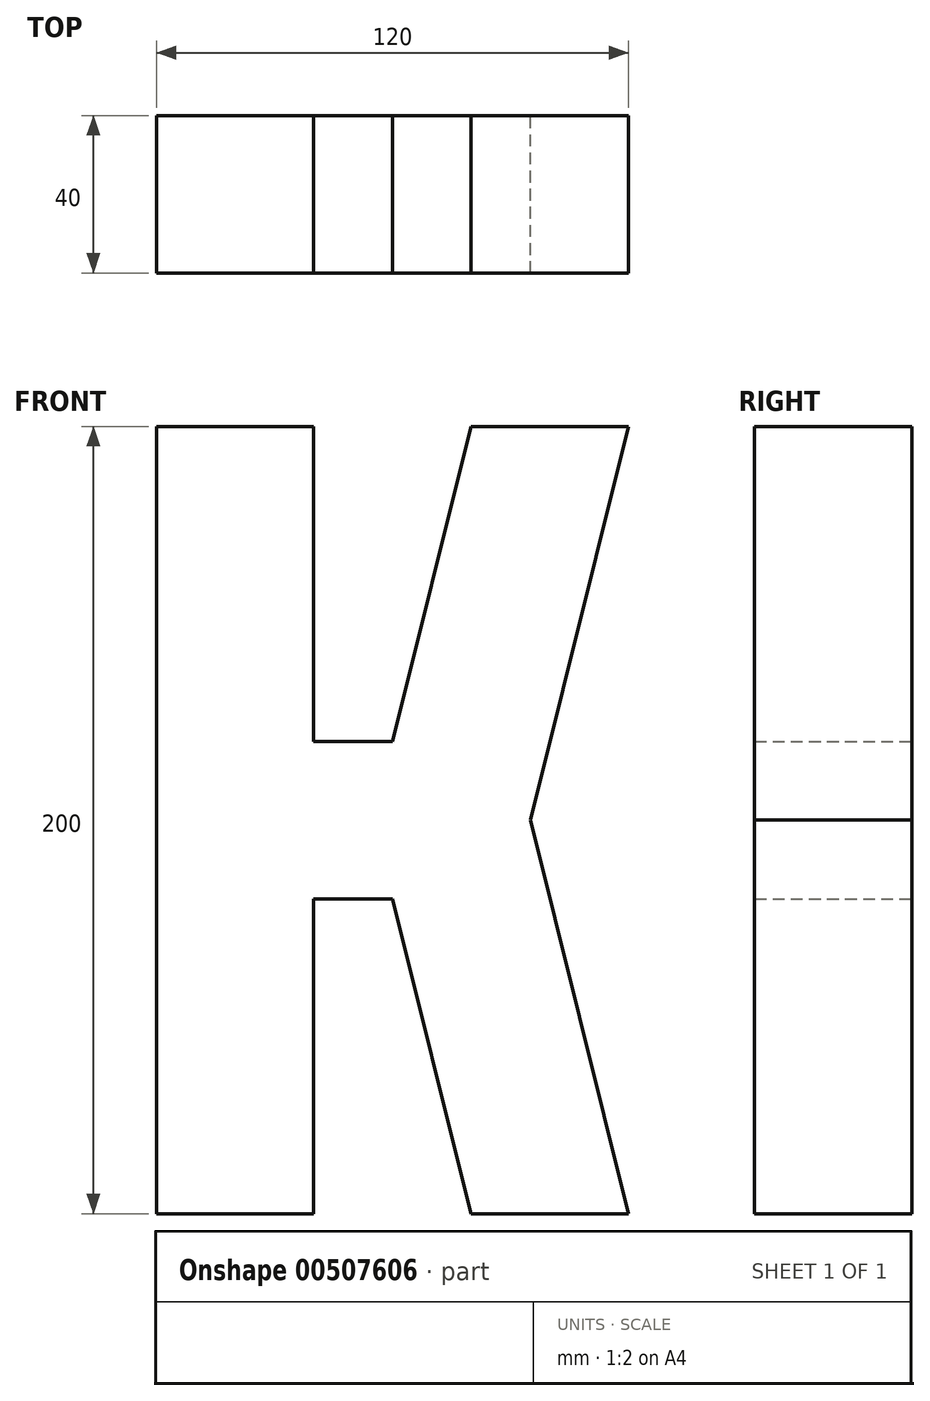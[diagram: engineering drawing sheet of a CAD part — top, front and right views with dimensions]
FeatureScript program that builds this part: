
annotation { "Feature Type Name" : "Feature", "Feature Type Description" : "" }
export const myFeature = defineFeature(function(context is Context, id is Id, definition is map)
    precondition{}
    {
        {
            var Q0;
            Q0=qCreatedBy(makeId("Front.planeOp"),FACE);
            var sketch = newSketch(context, id + "F0", { "sketchPlane" : qUnion([Q0])});
            skLineSegment(sketch, "E0.bottom", {"start": v(60, 100) * mm, "end": v(-60, 100) * mm});
            skLineSegment(sketch, "E0.top", {"start": v(60, -100) * mm, "end": v(-60, -100) * mm});
            skLineSegment(sketch, "E0.left", {"start": v(60, 100) * mm, "end": v(60, -100) * mm});
            skLineSegment(sketch, "E0.right", {"start": v(-60, 100) * mm, "end": v(-60, -100) * mm});
            skPoint(sketch, "E0.middle", {"position": v(0, 0) * mm});
            skLineSegment(sketch, "E1", {"start": v(-20, 100) * mm, "end": v(-20, -100) * mm});
            skLineSegment(sketch, "E2", {"start": v(20, 100) * mm, "end": v(20, -100) * mm});
            skLineSegment(sketch, "E3", {"start": v(60, 60) * mm, "end": v(-60, 60) * mm});
            skLineSegment(sketch, "E4", {"start": v(60, 20) * mm, "end": v(-60, 20) * mm});
            skLineSegment(sketch, "E5", {"start": v(60, -20) * mm, "end": v(-60, -20) * mm});
            skLineSegment(sketch, "E6", {"start": v(60, -60) * mm, "end": v(-60, -60) * mm});
            skPoint(sketch, "E7", {"position": v(0, 100) * mm});
            skLineSegment(sketch, "E8", {"start": v(0, 20) * mm, "end": v(20, 100) * mm});
            skLineSegment(sketch, "E9", {"start": v(60, 100) * mm, "end": v(35, 0) * mm});
            skLineSegment(sketch, "E10.MirrorCS", {"start": v(0, -20) * mm, "end": v(20, -100) * mm});
            skLineSegment(sketch, "E11.MirrorCS", {"start": v(60, -100) * mm, "end": v(35, 0) * mm});
            skSolve(sketch);
        }
        {
            var Q0;
            {var subQ0=sQuery(id+"F0.wireOp",EDGE,"E0.right");var subQ1=sQuery(id+"F0.wireOp",EDGE,"E0.bottom");var subQ2=makeQuery(id+"F0.imprint","INTERSECT",VERTEX,{"derivedFrom":[subQ1,subQ0]});Q0=makeQuery(id+"F0.imprint","IMPRINT",FACE,{"disambiguationData":[TD([[makeQuery(id+"F0.imprint","IMPRINT",EDGE,{"disambiguationData":[TD([[subQ2,1.0]])],"derivedFrom":subQ1}),1.0]])]});}
            var Q1;
            {var subQ0=sQuery(id+"F0.wireOp",EDGE,"E3");var subQ1=sQuery(id+"F0.wireOp",EDGE,"E0.right");var subQ2=makeQuery(id+"F0.imprint","INTERSECT",VERTEX,{"derivedFrom":[subQ1,subQ0]});Q1=makeQuery(id+"F0.imprint","IMPRINT",FACE,{"disambiguationData":[TD([[makeQuery(id+"F0.imprint","IMPRINT",EDGE,{"disambiguationData":[TD([[subQ2,-1.0]])],"derivedFrom":subQ1}),1.0]])]});}
            var Q2;
            {var subQ0=sQuery(id+"F0.wireOp",EDGE,"E4");var subQ1=sQuery(id+"F0.wireOp",EDGE,"E0.right");var subQ2=makeQuery(id+"F0.imprint","INTERSECT",VERTEX,{"derivedFrom":[subQ1,subQ0]});Q2=makeQuery(id+"F0.imprint","IMPRINT",FACE,{"disambiguationData":[TD([[makeQuery(id+"F0.imprint","IMPRINT",EDGE,{"disambiguationData":[TD([[subQ2,-1.0]])],"derivedFrom":subQ1}),1.0]])]});}
            var Q3;
            {var subQ0=sQuery(id+"F0.wireOp",EDGE,"E5");var subQ1=sQuery(id+"F0.wireOp",EDGE,"E0.right");var subQ2=makeQuery(id+"F0.imprint","INTERSECT",VERTEX,{"derivedFrom":[subQ1,subQ0]});Q3=makeQuery(id+"F0.imprint","IMPRINT",FACE,{"disambiguationData":[TD([[makeQuery(id+"F0.imprint","IMPRINT",EDGE,{"disambiguationData":[TD([[subQ2,-1.0]])],"derivedFrom":subQ1}),1.0]])]});}
            var Q4;
            {var subQ0=sQuery(id+"F0.wireOp",EDGE,"E0.right");var subQ1=sQuery(id+"F0.wireOp",EDGE,"E0.top");var subQ2=makeQuery(id+"F0.imprint","INTERSECT",VERTEX,{"derivedFrom":[subQ1,subQ0]});Q4=makeQuery(id+"F0.imprint","IMPRINT",FACE,{"disambiguationData":[TD([[makeQuery(id+"F0.imprint","IMPRINT",EDGE,{"disambiguationData":[TD([[subQ2,1.0]])],"derivedFrom":subQ1}),-1.0]])]});}
            var Q5;
            {var subQ0=sQuery(id+"F0.wireOp",EDGE,"E4");var subQ2=sQuery(id+"F0.wireOp",EDGE,"E1");var subQ3=makeQuery(id+"F0.imprint","INTERSECT",VERTEX,{"derivedFrom":[subQ2,subQ0]});Q5=makeQuery(id+"F0.imprint","IMPRINT",FACE,{"disambiguationData":[TD([[makeQuery(id+"F0.imprint","IMPRINT",EDGE,{"disambiguationData":[TD([[subQ3,-1.0]])],"derivedFrom":subQ2}),1.0]])]});}
            var Q6;
            {var subQ3=sQuery(id+"F0.wireOp",EDGE,"E4");var subQ6=sQuery(id+"F0.wireOp",EDGE,"E2");var subQ9=makeQuery(id+"F0.imprint","INTERSECT",VERTEX,{"derivedFrom":[subQ6,subQ3]});Q6=makeQuery(id+"F0.imprint","IMPRINT",FACE,{"disambiguationData":[TD([[makeQuery(id+"F0.imprint","IMPRINT",EDGE,{"disambiguationData":[TD([[subQ9,-1.0]])],"derivedFrom":subQ6}),1.0]])]});}
            var Q7;
            {var subQ0=sQuery(id+"F0.wireOp",EDGE,"E5");var subQ1=sQuery(id+"F0.wireOp",EDGE,"E2");var subQ2=makeQuery(id+"F0.imprint","INTERSECT",VERTEX,{"derivedFrom":[subQ1,subQ0]});Q7=makeQuery(id+"F0.imprint","IMPRINT",FACE,{"disambiguationData":[TD([[makeQuery(id+"F0.imprint","IMPRINT",EDGE,{"disambiguationData":[TD([[subQ2,-1.0]])],"derivedFrom":subQ1}),1.0]])]});}
            var Q8;
            {var subQ3=sQuery(id+"F0.wireOp",EDGE,"E2");var subQ5=sQuery(id+"F0.wireOp",EDGE,"E6");var subQ7=makeQuery(id+"F0.imprint","INTERSECT",VERTEX,{"derivedFrom":[subQ3,subQ5]});Q8=makeQuery(id+"F0.imprint","IMPRINT",FACE,{"disambiguationData":[TD([[makeQuery(id+"F0.imprint","IMPRINT",EDGE,{"disambiguationData":[TD([[subQ7,1.0]])],"derivedFrom":subQ5}),1.0]])]});}
            var Q9;
            {var subQ0=sQuery(id+"F0.wireOp",EDGE,"E5");var subQ1=sQuery(id+"F0.wireOp",EDGE,"E2");var subQ2=makeQuery(id+"F0.imprint","INTERSECT",VERTEX,{"derivedFrom":[subQ1,subQ0]});Q9=makeQuery(id+"F0.imprint","IMPRINT",FACE,{"disambiguationData":[TD([[makeQuery(id+"F0.imprint","IMPRINT",EDGE,{"disambiguationData":[TD([[subQ2,-1.0]])],"derivedFrom":subQ1}),-1.0]])]});}
            var Q10;
            {var subQ1=sQuery(id+"F0.wireOp",EDGE,"E2");var subQ3=sQuery(id+"F0.wireOp",EDGE,"E6");var subQ4=makeQuery(id+"F0.imprint","INTERSECT",VERTEX,{"derivedFrom":[subQ1,subQ3]});Q10=makeQuery(id+"F0.imprint","IMPRINT",FACE,{"disambiguationData":[TD([[makeQuery(id+"F0.imprint","IMPRINT",EDGE,{"disambiguationData":[TD([[subQ4,-1.0]])],"derivedFrom":subQ3}),1.0]])]});}
            var Q11;
            {var subQ0=sQuery(id+"F0.wireOp",EDGE,"E3");var subQ1=sQuery(id+"F0.wireOp",EDGE,"E2");var subQ2=makeQuery(id+"F0.imprint","INTERSECT",VERTEX,{"derivedFrom":[subQ1,subQ0]});Q11=makeQuery(id+"F0.imprint","IMPRINT",FACE,{"disambiguationData":[TD([[makeQuery(id+"F0.imprint","IMPRINT",EDGE,{"disambiguationData":[TD([[subQ2,-1.0]])],"derivedFrom":subQ1}),-1.0]])]});}
            var Q12;
            {var subQ0=sQuery(id+"F0.wireOp",EDGE,"E3");var subQ1=sQuery(id+"F0.wireOp",EDGE,"E2");var subQ2=makeQuery(id+"F0.imprint","INTERSECT",VERTEX,{"derivedFrom":[subQ1,subQ0]});Q12=makeQuery(id+"F0.imprint","IMPRINT",FACE,{"disambiguationData":[TD([[makeQuery(id+"F0.imprint","IMPRINT",EDGE,{"disambiguationData":[TD([[subQ2,-1.0]])],"derivedFrom":subQ1}),1.0]])]});}
            var Q13;
            {var subQ3=sQuery(id+"F0.wireOp",EDGE,"E2");var subQ5=sQuery(id+"F0.wireOp",EDGE,"E3");var subQ6=makeQuery(id+"F0.imprint","INTERSECT",VERTEX,{"derivedFrom":[subQ3,subQ5]});Q13=makeQuery(id+"F0.imprint","IMPRINT",FACE,{"disambiguationData":[TD([[makeQuery(id+"F0.imprint","IMPRINT",EDGE,{"disambiguationData":[TD([[subQ6,1.0]])],"derivedFrom":subQ5}),-1.0]])]});}
            var Q14;
            {var subQ1=sQuery(id+"F0.wireOp",EDGE,"E2");var subQ3=sQuery(id+"F0.wireOp",EDGE,"E3");var subQ4=makeQuery(id+"F0.imprint","INTERSECT",VERTEX,{"derivedFrom":[subQ1,subQ3]});Q14=makeQuery(id+"F0.imprint","IMPRINT",FACE,{"disambiguationData":[TD([[makeQuery(id+"F0.imprint","IMPRINT",EDGE,{"disambiguationData":[TD([[subQ4,-1.0]])],"derivedFrom":subQ3}),-1.0]])]});}
            extrude(context, id + "F1", {"entities" : qUnion([Q0, Q1, Q2, Q3, Q4, Q5, Q6, Q7, Q8, Q9, Q10, Q11, Q12, Q13, Q14]), "depth" : 40 * mm, "offsetDistance" : 25 * mm});
        }
    });
